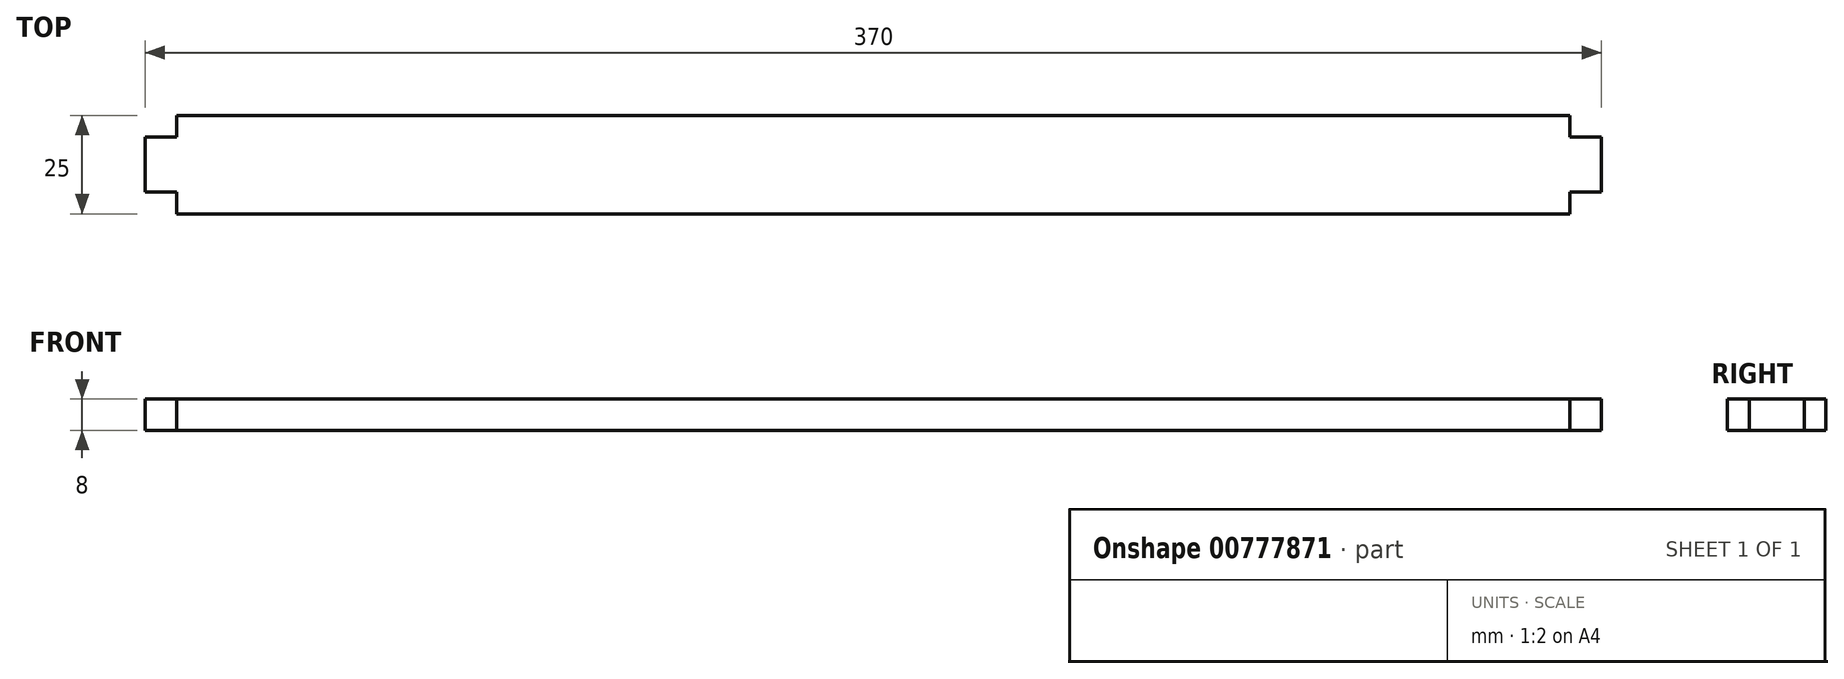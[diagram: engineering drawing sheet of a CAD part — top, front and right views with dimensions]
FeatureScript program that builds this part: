
annotation { "Feature Type Name" : "Feature", "Feature Type Description" : "" }
export const myFeature = defineFeature(function(context is Context, id is Id, definition is map)
    precondition{}
    {
        {
            var Q0;
            Q0=qCreatedBy(makeId("Top.planeOp"),FACE);
            var sketch = newSketch(context, id + "F0", { "sketchPlane" : qUnion([Q0])});
            skLineSegment(sketch, "E0.bottom", {"start": v(-185, 12.5) * mm, "end": v(185, 12.5) * mm});
            skLineSegment(sketch, "E0.top", {"start": v(-185, -12.5) * mm, "end": v(185, -12.5) * mm});
            skLineSegment(sketch, "E0.left", {"start": v(-185, 12.5) * mm, "end": v(-185, -12.5) * mm});
            skLineSegment(sketch, "E0.right", {"start": v(185, 12.5) * mm, "end": v(185, -12.5) * mm});
            skSolve(sketch);
        }
        {
            var Q0;
            Q0 = qSketchRegion(id + "F0", true);
            extrude(context, id + "F1", {"entities" : qUnion([Q0]), "endBound" : BoundingType.SYMMETRIC, "depth" : 8 * mm, "offsetDistance" : 25 * mm});
        }
        {
            var Q0;
            Q0=makeQuery(id+"F1.opExtrude","CAP_FACE",FACE,{"disambiguationData":[OSD([sQuery(id+"F0.wireOp",EDGE,"E0.bottom"),sQuery(id+"F0.wireOp",EDGE,"E0.top"),sQuery(id+"F0.wireOp",EDGE,"E0.left"),sQuery(id+"F0.wireOp",EDGE,"E0.right")])],"isStart":false});
            var sketch = newSketch(context, id + "F2", { "sketchPlane" : qUnion([Q0])});
            skLineSegment(sketch, "E1.bottom", {"start": v(-185, 12.5) * mm, "end": v(-177, 12.5) * mm});
            skLineSegment(sketch, "E1.top", {"start": v(-185, 7) * mm, "end": v(-177, 7) * mm});
            skLineSegment(sketch, "E1.left", {"start": v(-185, 12.5) * mm, "end": v(-185, 7) * mm});
            skLineSegment(sketch, "E1.right", {"start": v(-177, 12.5) * mm, "end": v(-177, 7) * mm});
            skLineSegment(sketch, "E2.bottom", {"start": v(-185, -12.5) * mm, "end": v(-177, -12.5) * mm});
            skLineSegment(sketch, "E2.top", {"start": v(-185, -7) * mm, "end": v(-177, -7) * mm});
            skLineSegment(sketch, "E2.left", {"start": v(-185, -12.5) * mm, "end": v(-185, -7) * mm});
            skLineSegment(sketch, "E2.right", {"start": v(-177, -12.5) * mm, "end": v(-177, -7) * mm});
            skLineSegment(sketch, "E3.bottom", {"start": v(185, 12.5) * mm, "end": v(177, 12.5) * mm});
            skLineSegment(sketch, "E3.top", {"start": v(185, 7) * mm, "end": v(177, 7) * mm});
            skLineSegment(sketch, "E3.left", {"start": v(185, 12.5) * mm, "end": v(185, 7) * mm});
            skLineSegment(sketch, "E3.right", {"start": v(177, 12.5) * mm, "end": v(177, 7) * mm});
            skLineSegment(sketch, "E4.bottom", {"start": v(185, -12.5) * mm, "end": v(177, -12.5) * mm});
            skLineSegment(sketch, "E4.top", {"start": v(185, -7) * mm, "end": v(177, -7) * mm});
            skLineSegment(sketch, "E4.left", {"start": v(185, -12.5) * mm, "end": v(185, -7) * mm});
            skLineSegment(sketch, "E4.right", {"start": v(177, -12.5) * mm, "end": v(177, -7) * mm});
            skSolve(sketch);
        }
        {
            var Q0;
            Q0 = qSketchRegion(id + "F2", true);
            extrude(context, id + "F3", {"entities" : qUnion([Q0]), "operationType" : NewBodyOperationType.REMOVE, "oppositeDirection" : true, "depth" : 8 * mm, "offsetDistance" : 25 * mm});
        }
    });
